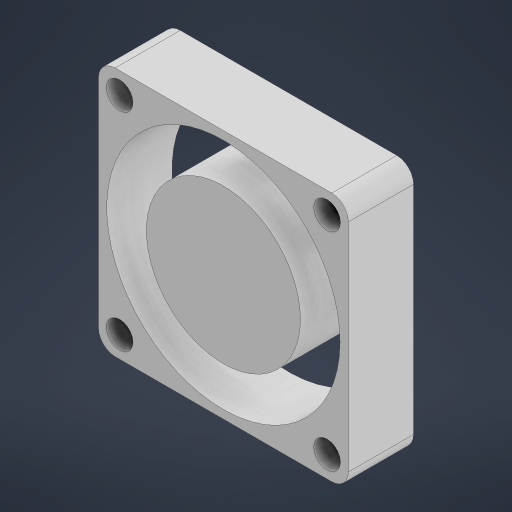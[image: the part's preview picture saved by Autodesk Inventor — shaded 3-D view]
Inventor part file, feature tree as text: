
AUTODESK INVENTOR PART (.ipt)
format: ipt  version: 2024 (Build 280153000, 153)  size: 208,384 bytes
history: native  units: in
note: dims shown in document units (in); Inventor stores cm internally (conversion verified against a paired STEP export)
features: extrude x1, fillet x1, sketch x1
ambient origin geometry x8: Origin, YZ Plane, XZ Plane, XY Plane, X Axis, Y Axis, Z Axis, Center Point
bodies: Solid1 (feature_tree)
feature tree (3):
  extrude  "Extrusion1"  Depth=1.1811in
  fillet  "Fillet1"  Radius=0.126in
  sketch  "Sketch1"  dims[d0=1.1811in d1=1.1811in d2=0.126in d3=0.1004in d4=0.1004in d5=1.1024in d6=0.7283in d7=0.3079in d8=0.0in d9=0.0787in]
